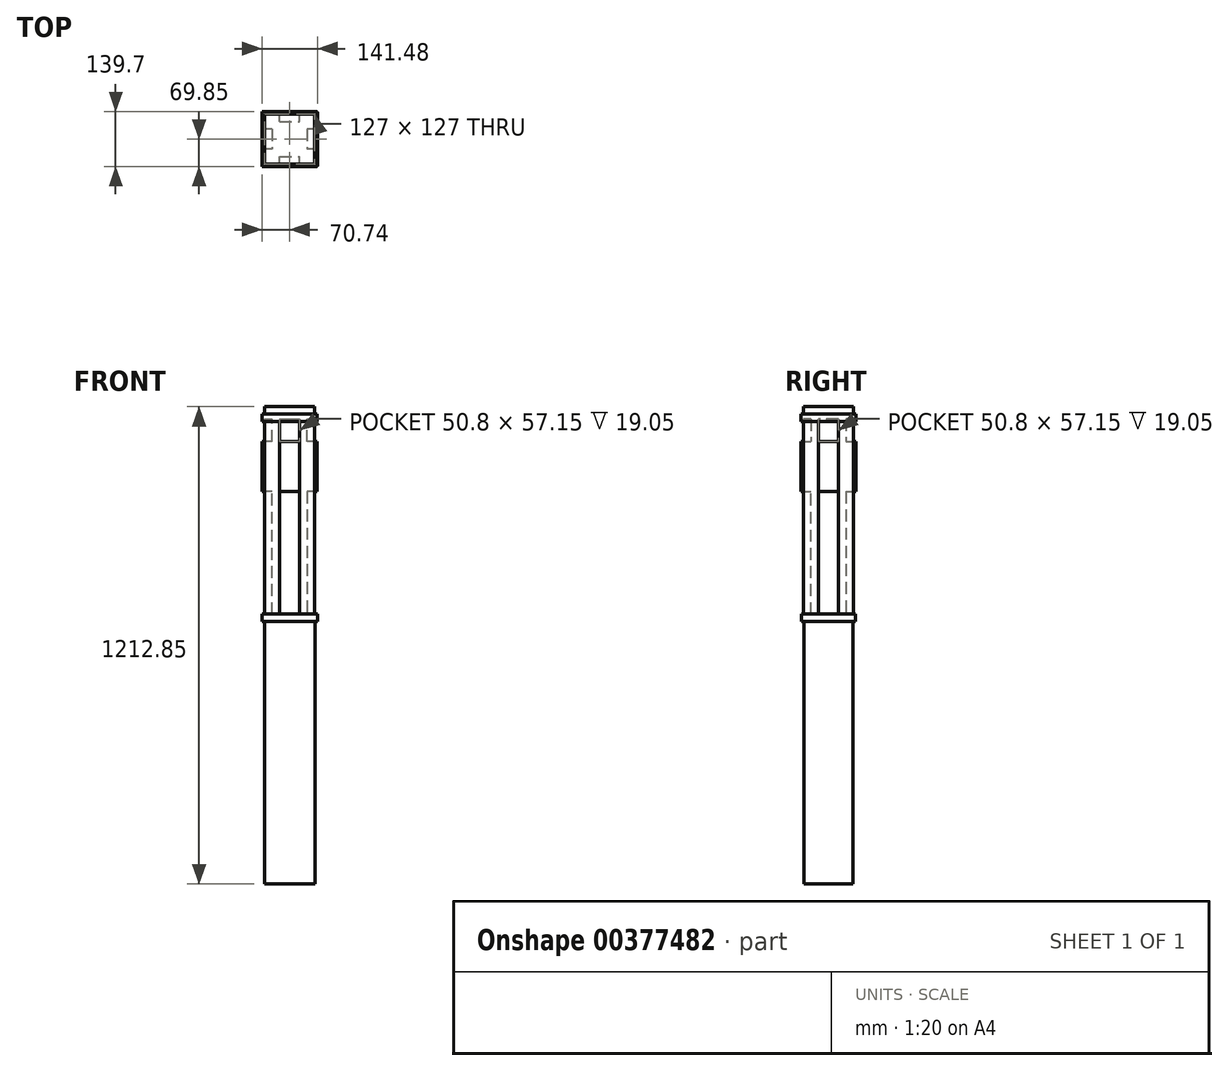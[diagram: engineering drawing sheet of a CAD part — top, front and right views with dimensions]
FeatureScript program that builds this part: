
annotation { "Feature Type Name" : "Feature", "Feature Type Description" : "" }
export const myFeature = defineFeature(function(context is Context, id is Id, definition is map)
    precondition{}
    {
        {
            var Q0;
            Q0=qCreatedBy(makeId("Top.planeOp"),FACE);
            var sketch = newSketch(context, id + "F0", { "sketchPlane" : qUnion([Q0])});
            skLineSegment(sketch, "E0.bottom", {"start": v(-64.39, 62.74) * mm, "end": v(64.39, 62.74) * mm});
            skLineSegment(sketch, "E0.top", {"start": v(-64.39, -62.74) * mm, "end": v(64.39, -62.74) * mm});
            skLineSegment(sketch, "E0.left", {"start": v(-64.39, 62.74) * mm, "end": v(-64.39, -62.74) * mm});
            skLineSegment(sketch, "E0.right", {"start": v(64.39, 62.74) * mm, "end": v(64.39, -62.74) * mm});
            skPoint(sketch, "E0.middle", {"position": v(0, 0) * mm});
            skSolve(sketch);
        }
        {
            var Q0;
            Q0 = qSketchRegion(id + "F0", true);
            extrude(context, id + "F1", {"entities" : qUnion([Q0]), "depth" : 673.1 * mm, "offsetDistance" : 25.4 * mm});
        }
        {
            var Q0;
            Q0=makeQuery(id+"F1.opExtrude","CAP_FACE",FACE,{"disambiguationData":[OSD([sQuery(id+"F0.wireOp",EDGE,"E0.bottom"),sQuery(id+"F0.wireOp",EDGE,"E0.top"),sQuery(id+"F0.wireOp",EDGE,"E0.left"),sQuery(id+"F0.wireOp",EDGE,"E0.right")])],"isStart":false});
            var sketch = newSketch(context, id + "F2", { "sketchPlane" : qUnion([Q0])});
            skLineSegment(sketch, "E1.bottom", {"start": v(-44.45, 44.45) * mm, "end": v(44.45, 44.45) * mm});
            skLineSegment(sketch, "E1.top", {"start": v(-44.45, -44.45) * mm, "end": v(44.45, -44.45) * mm});
            skLineSegment(sketch, "E1.left", {"start": v(-44.45, 44.45) * mm, "end": v(-44.45, -44.45) * mm});
            skLineSegment(sketch, "E1.right", {"start": v(44.45, 44.45) * mm, "end": v(44.45, -44.45) * mm});
            skPoint(sketch, "E1.middle", {"position": v(0, 0) * mm});
            skSolve(sketch);
        }
        {
            var Q0;
            Q0 = qSketchRegion(id + "F2", true);
            extrude(context, id + "F3", {"entities" : qUnion([Q0]), "operationType" : NewBodyOperationType.ADD, "depth" : 508 * mm, "offsetDistance" : 25.4 * mm});
        }
        {
            var Q0;
            Q0=makeQuery(id+"F1.opExtrude","CAP_FACE",FACE,{"disambiguationData":[OSD([sQuery(id+"F0.wireOp",EDGE,"E0.bottom"),sQuery(id+"F0.wireOp",EDGE,"E0.top"),sQuery(id+"F0.wireOp",EDGE,"E0.left"),sQuery(id+"F0.wireOp",EDGE,"E0.right")])],"isStart":false});
            var sketch = newSketch(context, id + "F4", { "sketchPlane" : qUnion([Q0])});
            skLineSegment(sketch, "E2.bottom", {"start": v(-44.45, 44.45) * mm, "end": v(44.45, 44.45) * mm});
            skLineSegment(sketch, "E2.top", {"start": v(-44.45, -44.45) * mm, "end": v(44.45, -44.45) * mm});
            skLineSegment(sketch, "E2.left", {"start": v(-44.45, 44.45) * mm, "end": v(-44.45, -44.45) * mm});
            skLineSegment(sketch, "E2.right", {"start": v(44.45, 44.45) * mm, "end": v(44.45, -44.45) * mm});
            skPoint(sketch, "E2.middle", {"position": v(0, 0) * mm});
            skLineSegment(sketch, "E3.0", {"start": v(-70.74, 69.09) * mm, "end": v(70.74, 69.09) * mm});
            skLineSegment(sketch, "E3.1", {"start": v(-70.74, 69.09) * mm, "end": v(-70.74, -69.09) * mm});
            skLineSegment(sketch, "E3.2", {"start": v(-70.74, -69.09) * mm, "end": v(70.74, -69.09) * mm});
            skLineSegment(sketch, "E3.3", {"start": v(70.74, 69.09) * mm, "end": v(70.74, -69.09) * mm});
            skSolve(sketch);
        }
        {
            var Q0;
            Q0 = qSketchRegion(id + "F4", true);
            extrude(context, id + "F5", {"entities" : qUnion([Q0]), "operationType" : NewBodyOperationType.ADD, "depth" : 12.7 * mm, "offsetDistance" : 25.4 * mm});
        }
        {
            var Q0;
            Q0=makeQuery(id+"F5.opExtrude","CAP_FACE",FACE,{"disambiguationData":[OSD([sQuery(id+"F4.wireOp",EDGE,"E2.bottom"),sQuery(id+"F4.wireOp",EDGE,"E2.top"),sQuery(id+"F4.wireOp",EDGE,"E2.left"),sQuery(id+"F4.wireOp",EDGE,"E2.right"),sQuery(id+"F4.wireOp",EDGE,"E3.0"),sQuery(id+"F4.wireOp",EDGE,"E3.1"),sQuery(id+"F4.wireOp",EDGE,"E3.2"),sQuery(id+"F4.wireOp",EDGE,"E3.3")])],"isStart":true});
            var sketch = newSketch(context, id + "F6", { "sketchPlane" : qUnion([Q0])});
            skLineSegment(sketch, "E4.bottom", {"start": v(-64.39, 62.74) * mm, "end": v(64.39, 62.74) * mm});
            skLineSegment(sketch, "E4.top", {"start": v(-64.39, -62.74) * mm, "end": v(64.39, -62.74) * mm});
            skLineSegment(sketch, "E4.left", {"start": v(-64.39, 62.74) * mm, "end": v(-64.39, -62.74) * mm});
            skLineSegment(sketch, "E4.right", {"start": v(64.39, 62.74) * mm, "end": v(64.39, -62.74) * mm});
            skPoint(sketch, "E4.middle", {"position": v(0, 0) * mm});
            skLineSegment(sketch, "E5.bottom", {"start": v(-70.74, 69.09) * mm, "end": v(70.74, 69.09) * mm});
            skLineSegment(sketch, "E5.top", {"start": v(-70.74, -69.09) * mm, "end": v(70.74, -69.09) * mm});
            skLineSegment(sketch, "E5.left", {"start": v(-70.74, 69.09) * mm, "end": v(-70.74, -69.09) * mm});
            skLineSegment(sketch, "E5.right", {"start": v(70.74, 69.09) * mm, "end": v(70.74, -69.09) * mm});
            skSolve(sketch);
        }
        {
            var Q0;
            Q0 = qSketchRegion(id + "F6", true);
            extrude(context, id + "F7", {"entities" : qUnion([Q0]), "operationType" : NewBodyOperationType.ADD, "depth" : 6.35 * mm, "offsetDistance" : 25.4 * mm});
        }
        {
            var Q0;
            Q0=makeQuery(id+"F5.opExtrude","CAP_FACE",FACE,{"disambiguationData":[OSD([sQuery(id+"F4.wireOp",EDGE,"E2.bottom"),sQuery(id+"F4.wireOp",EDGE,"E2.top"),sQuery(id+"F4.wireOp",EDGE,"E2.left"),sQuery(id+"F4.wireOp",EDGE,"E2.right"),sQuery(id+"F4.wireOp",EDGE,"E3.0"),sQuery(id+"F4.wireOp",EDGE,"E3.1"),sQuery(id+"F4.wireOp",EDGE,"E3.2"),sQuery(id+"F4.wireOp",EDGE,"E3.3")])],"isStart":false});
            var sketch = newSketch(context, id + "F8", { "sketchPlane" : qUnion([Q0])});
            skLineSegment(sketch, "E6.bottom", {"start": v(63.5, 63.5) * mm, "end": v(25.4, 63.5) * mm});
            skLineSegment(sketch, "E6.top", {"start": v(63.5, 25.4) * mm, "end": v(25.4, 25.4) * mm});
            skLineSegment(sketch, "E6.left", {"start": v(63.5, 63.5) * mm, "end": v(63.5, 25.4) * mm});
            skLineSegment(sketch, "E6.right", {"start": v(25.4, 63.5) * mm, "end": v(25.4, 25.4) * mm});
            skPoint(sketch, "E6.middle", {"position": v(44.45, 44.45) * mm});
            skLineSegment(sketch, "E7.bottom", {"start": v(25.4, -25.4) * mm, "end": v(63.5, -25.4) * mm});
            skLineSegment(sketch, "E7.top", {"start": v(25.4, -63.5) * mm, "end": v(63.5, -63.5) * mm});
            skLineSegment(sketch, "E7.left", {"start": v(25.4, -25.4) * mm, "end": v(25.4, -63.5) * mm});
            skLineSegment(sketch, "E7.right", {"start": v(63.5, -25.4) * mm, "end": v(63.5, -63.5) * mm});
            skPoint(sketch, "E7.middle", {"position": v(44.45, -44.45) * mm});
            skLineSegment(sketch, "E8.bottom", {"start": v(-63.5, -63.5) * mm, "end": v(-25.4, -63.5) * mm});
            skLineSegment(sketch, "E8.top", {"start": v(-63.5, -25.4) * mm, "end": v(-25.4, -25.4) * mm});
            skLineSegment(sketch, "E8.left", {"start": v(-63.5, -63.5) * mm, "end": v(-63.5, -25.4) * mm});
            skLineSegment(sketch, "E8.right", {"start": v(-25.4, -63.5) * mm, "end": v(-25.4, -25.4) * mm});
            skPoint(sketch, "E8.middle", {"position": v(-44.45, -44.45) * mm});
            skLineSegment(sketch, "E9.bottom", {"start": v(-63.5, 63.5) * mm, "end": v(-25.4, 63.5) * mm});
            skLineSegment(sketch, "E9.top", {"start": v(-63.5, 25.4) * mm, "end": v(-25.4, 25.4) * mm});
            skLineSegment(sketch, "E9.left", {"start": v(-63.5, 63.5) * mm, "end": v(-63.5, 25.4) * mm});
            skLineSegment(sketch, "E9.right", {"start": v(-25.4, 63.5) * mm, "end": v(-25.4, 25.4) * mm});
            skPoint(sketch, "E9.middle", {"position": v(-44.45, 44.45) * mm});
            skSolve(sketch);
        }
        {
            var Q0;
            Q0 = qSketchRegion(id + "F8", true);
            extrude(context, id + "F9", {"entities" : qUnion([Q0]), "operationType" : NewBodyOperationType.ADD, "depth" : 495.3 * mm, "offsetDistance" : 25.4 * mm});
        }
        {
            var Q0;
            Q0=makeQuery(id+"F9.boolean.opBoolean","MERGE",FACE,{"derivedFrom":[makeQuery(id+"F3.opExtrude","CAP_FACE",FACE,{"disambiguationData":[OSD([sQuery(id+"F2.wireOp",EDGE,"E1.bottom"),sQuery(id+"F2.wireOp",EDGE,"E1.top"),sQuery(id+"F2.wireOp",EDGE,"E1.left"),sQuery(id+"F2.wireOp",EDGE,"E1.right")])],"isStart":false}),makeQuery(id+"F9.opExtrude","CAP_FACE",FACE,{"disambiguationData":[OSD([sQuery(id+"F8.wireOp",EDGE,"E6.bottom"),sQuery(id+"F8.wireOp",EDGE,"E6.top"),sQuery(id+"F8.wireOp",EDGE,"E6.left"),sQuery(id+"F8.wireOp",EDGE,"E6.right")])],"isStart":false}),makeQuery(id+"F9.opExtrude","CAP_FACE",FACE,{"disambiguationData":[OSD([sQuery(id+"F8.wireOp",EDGE,"E7.bottom"),sQuery(id+"F8.wireOp",EDGE,"E7.top"),sQuery(id+"F8.wireOp",EDGE,"E7.left"),sQuery(id+"F8.wireOp",EDGE,"E7.right")])],"isStart":false}),makeQuery(id+"F9.opExtrude","CAP_FACE",FACE,{"disambiguationData":[OSD([sQuery(id+"F8.wireOp",EDGE,"E8.bottom"),sQuery(id+"F8.wireOp",EDGE,"E8.top"),sQuery(id+"F8.wireOp",EDGE,"E8.left"),sQuery(id+"F8.wireOp",EDGE,"E8.right")])],"isStart":false}),makeQuery(id+"F9.opExtrude","CAP_FACE",FACE,{"disambiguationData":[OSD([sQuery(id+"F8.wireOp",EDGE,"E9.bottom"),sQuery(id+"F8.wireOp",EDGE,"E9.top"),sQuery(id+"F8.wireOp",EDGE,"E9.left"),sQuery(id+"F8.wireOp",EDGE,"E9.right")])],"isStart":false})]});
            var sketch = newSketch(context, id + "F10", { "sketchPlane" : qUnion([Q0])});
            skLineSegment(sketch, "E10.bottom", {"start": v(-63.5, -63.5) * mm, "end": v(63.5, -63.5) * mm});
            skLineSegment(sketch, "E10.top", {"start": v(-63.5, 63.5) * mm, "end": v(63.5, 63.5) * mm});
            skLineSegment(sketch, "E10.left", {"start": v(-63.5, -63.5) * mm, "end": v(-63.5, 63.5) * mm});
            skLineSegment(sketch, "E10.right", {"start": v(63.5, -63.5) * mm, "end": v(63.5, 63.5) * mm});
            skPoint(sketch, "E10.middle", {"position": v(0, 0) * mm});
            skLineSegment(sketch, "E11.0", {"start": v(-69.85, 69.85) * mm, "end": v(69.85, 69.85) * mm});
            skLineSegment(sketch, "E11.1", {"start": v(-69.85, -69.85) * mm, "end": v(-69.85, 69.85) * mm});
            skLineSegment(sketch, "E11.2", {"start": v(-69.85, -69.85) * mm, "end": v(69.85, -69.85) * mm});
            skLineSegment(sketch, "E11.3", {"start": v(69.85, -69.85) * mm, "end": v(69.85, 69.85) * mm});
            skSolve(sketch);
        }
        {
            var Q0;
            Q0 = qSketchRegion(id + "F10", true);
            extrude(context, id + "F11", {"entities" : qUnion([Q0]), "operationType" : NewBodyOperationType.ADD, "oppositeDirection" : true, "depth" : 6.35 * mm, "offsetDistance" : 25.4 * mm});
        }
        {
            var Q0;
            Q0=makeQuery(id+"F11.boolean.opBoolean","MERGE",FACE,{"derivedFrom":[makeQuery(id+"F9.boolean.opBoolean","MERGE",FACE,{"derivedFrom":[makeQuery(id+"F3.opExtrude","CAP_FACE",FACE,{"disambiguationData":[OSD([sQuery(id+"F2.wireOp",EDGE,"E1.bottom"),sQuery(id+"F2.wireOp",EDGE,"E1.top"),sQuery(id+"F2.wireOp",EDGE,"E1.left"),sQuery(id+"F2.wireOp",EDGE,"E1.right")])],"isStart":false}),makeQuery(id+"F9.opExtrude","CAP_FACE",FACE,{"disambiguationData":[OSD([sQuery(id+"F8.wireOp",EDGE,"E6.bottom"),sQuery(id+"F8.wireOp",EDGE,"E6.top"),sQuery(id+"F8.wireOp",EDGE,"E6.left"),sQuery(id+"F8.wireOp",EDGE,"E6.right")])],"isStart":false}),makeQuery(id+"F9.opExtrude","CAP_FACE",FACE,{"disambiguationData":[OSD([sQuery(id+"F8.wireOp",EDGE,"E7.bottom"),sQuery(id+"F8.wireOp",EDGE,"E7.top"),sQuery(id+"F8.wireOp",EDGE,"E7.left"),sQuery(id+"F8.wireOp",EDGE,"E7.right")])],"isStart":false}),makeQuery(id+"F9.opExtrude","CAP_FACE",FACE,{"disambiguationData":[OSD([sQuery(id+"F8.wireOp",EDGE,"E8.bottom"),sQuery(id+"F8.wireOp",EDGE,"E8.top"),sQuery(id+"F8.wireOp",EDGE,"E8.left"),sQuery(id+"F8.wireOp",EDGE,"E8.right")])],"isStart":false}),makeQuery(id+"F9.opExtrude","CAP_FACE",FACE,{"disambiguationData":[OSD([sQuery(id+"F8.wireOp",EDGE,"E9.bottom"),sQuery(id+"F8.wireOp",EDGE,"E9.top"),sQuery(id+"F8.wireOp",EDGE,"E9.left"),sQuery(id+"F8.wireOp",EDGE,"E9.right")])],"isStart":false})]}),makeQuery(id+"F11.opExtrude","CAP_FACE",FACE,{"disambiguationData":[OSD([sQuery(id+"F10.wireOp",EDGE,"E10.bottom"),sQuery(id+"F10.wireOp",EDGE,"E10.top"),sQuery(id+"F10.wireOp",EDGE,"E10.left"),sQuery(id+"F10.wireOp",EDGE,"E10.right"),sQuery(id+"F10.wireOp",EDGE,"E11.0"),sQuery(id+"F10.wireOp",EDGE,"E11.1"),sQuery(id+"F10.wireOp",EDGE,"E11.2"),sQuery(id+"F10.wireOp",EDGE,"E11.3")])],"isStart":true})]});
            var sketch = newSketch(context, id + "F12", { "sketchPlane" : qUnion([Q0])});
            skLineSegment(sketch, "E12.bottom", {"start": v(-69.85, 69.85) * mm, "end": v(69.85, 69.85) * mm});
            skLineSegment(sketch, "E12.top", {"start": v(-69.85, -69.85) * mm, "end": v(69.85, -69.85) * mm});
            skLineSegment(sketch, "E12.left", {"start": v(-69.85, 69.85) * mm, "end": v(-69.85, -69.85) * mm});
            skLineSegment(sketch, "E12.right", {"start": v(69.85, 69.85) * mm, "end": v(69.85, -69.85) * mm});
            skPoint(sketch, "E12.middle", {"position": v(0, 0) * mm});
            skSolve(sketch);
        }
        {
            var Q0;
            Q0 = qSketchRegion(id + "F12", true);
            extrude(context, id + "F13", {"entities" : qUnion([Q0]), "operationType" : NewBodyOperationType.ADD, "depth" : 12.7 * mm, "offsetDistance" : 25.4 * mm});
        }
        {
            var Q0;
            Q0=makeQuery(id+"F3.opExtrude","SWEPT_FACE",FACE,{"disambiguationData":[OSD([sQuery(id+"F2.wireOp",EDGE,"E1.top")])]});
            var sketch = newSketch(context, id + "F14", { "sketchPlane" : qUnion([Q0])});
            skLineSegment(sketch, "E13.bottom", {"start": v(-25.4, 1123.95) * mm, "end": v(25.4, 1123.95) * mm});
            skLineSegment(sketch, "E13.top", {"start": v(-25.4, 996.95) * mm, "end": v(25.4, 996.95) * mm});
            skLineSegment(sketch, "E13.left", {"start": v(-25.4, 1123.95) * mm, "end": v(-25.4, 996.95) * mm});
            skLineSegment(sketch, "E13.right", {"start": v(25.4, 1123.95) * mm, "end": v(25.4, 996.95) * mm});
            skSolve(sketch);
        }
        {
            var Q0;
            Q0 = qSketchRegion(id + "F14", true);
            extrude(context, id + "F15", {"entities" : qUnion([Q0]), "operationType" : NewBodyOperationType.ADD, "depth" : 25.4 * mm, "offsetDistance" : 25.4 * mm, "hasSecondDirection" : true, "secondDirectionOppositeDirection" : true, "secondDirectionDepth" : 114.3 * mm});
        }
        {
            var Q0;
            Q0=makeQuery(id+"F3.opExtrude","SWEPT_FACE",FACE,{"disambiguationData":[OSD([sQuery(id+"F2.wireOp",EDGE,"E1.right")])]});
            var sketch = newSketch(context, id + "F16", { "sketchPlane" : qUnion([Q0])});
            skLineSegment(sketch, "E14.bottom", {"start": v(-25.4, 1123.95) * mm, "end": v(25.4, 1123.95) * mm});
            skLineSegment(sketch, "E14.top", {"start": v(-25.4, 996.95) * mm, "end": v(25.4, 996.95) * mm});
            skLineSegment(sketch, "E14.left", {"start": v(-25.4, 1123.95) * mm, "end": v(-25.4, 996.95) * mm});
            skLineSegment(sketch, "E14.right", {"start": v(25.4, 1123.95) * mm, "end": v(25.4, 996.95) * mm});
            skSolve(sketch);
        }
        {
            var Q0;
            Q0 = qSketchRegion(id + "F16", true);
            extrude(context, id + "F17", {"entities" : qUnion([Q0]), "operationType" : NewBodyOperationType.ADD, "depth" : 25.4 * mm, "offsetDistance" : 25.4 * mm, "hasSecondDirection" : true, "secondDirectionOppositeDirection" : true, "secondDirectionDepth" : 114.3 * mm});
        }
        {
            var Q0;
            Q0=makeQuery(id+"F13.opExtrude","CAP_FACE",FACE,{"disambiguationData":[OSD([sQuery(id+"F12.wireOp",EDGE,"E12.bottom"),sQuery(id+"F12.wireOp",EDGE,"E12.top"),sQuery(id+"F12.wireOp",EDGE,"E12.left"),sQuery(id+"F12.wireOp",EDGE,"E12.right")])],"isStart":false});
            var sketch = newSketch(context, id + "F18", { "sketchPlane" : qUnion([Q0])});
            skLineSegment(sketch, "E15.0", {"start": v(-63.5, 63.5) * mm, "end": v(63.5, 63.5) * mm});
            skLineSegment(sketch, "E15.1", {"start": v(-63.5, -63.5) * mm, "end": v(-63.5, 63.5) * mm});
            skLineSegment(sketch, "E15.2", {"start": v(-63.5, -63.5) * mm, "end": v(63.5, -63.5) * mm});
            skLineSegment(sketch, "E15.3", {"start": v(63.5, -63.5) * mm, "end": v(63.5, 63.5) * mm});
            skSolve(sketch);
        }
        {
            var Q0;
            Q0 = qSketchRegion(id + "F18", true);
            extrude(context, id + "F19", {"entities" : qUnion([Q0]), "operationType" : NewBodyOperationType.ADD, "depth" : 19.05 * mm, "offsetDistance" : 25.4 * mm});
        }
    });
